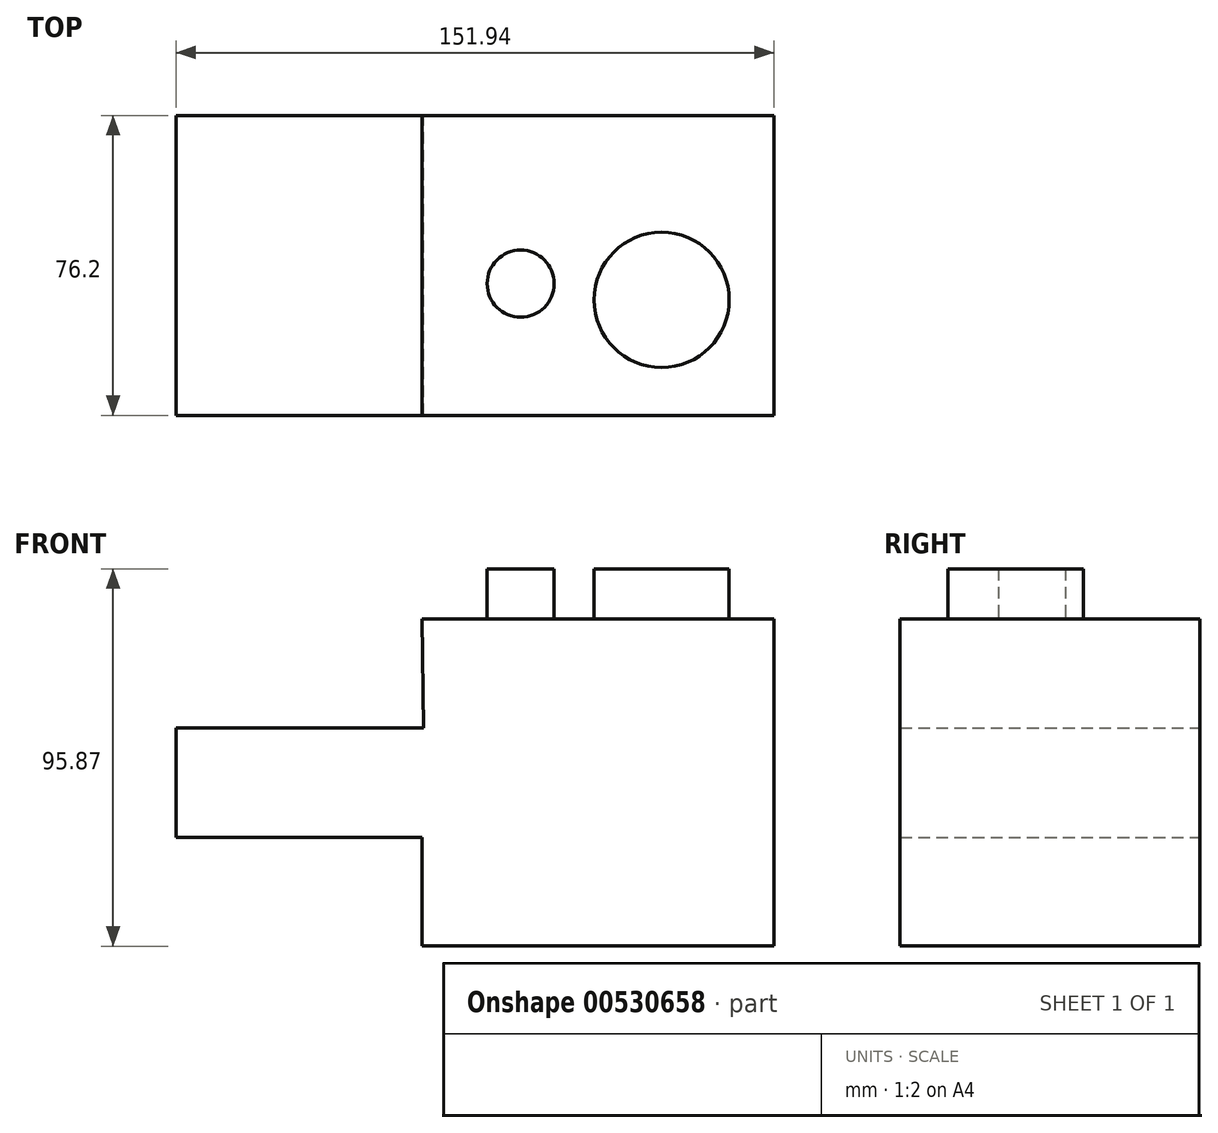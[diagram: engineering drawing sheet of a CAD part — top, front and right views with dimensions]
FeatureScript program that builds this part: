
annotation { "Feature Type Name" : "Feature", "Feature Type Description" : "" }
export const myFeature = defineFeature(function(context is Context, id is Id, definition is map)
    precondition{}
    {
        {
            var Q0;
            Q0=qCreatedBy(makeId("Front.planeOp"),FACE);
            var sketch = newSketch(context, id + "F0", { "sketchPlane" : qUnion([Q0])});
            skLineSegment(sketch, "E0.bottom", {"start": v(-81.39, 11.43) * mm, "end": v(-18.52, 11.43) * mm});
            skLineSegment(sketch, "E0.top", {"start": v(-81.39, -16.36) * mm, "end": v(-18.52, -16.36) * mm});
            skLineSegment(sketch, "E0.left", {"start": v(-81.39, 11.43) * mm, "end": v(-81.39, -16.36) * mm});
            skLineSegment(sketch, "E1.bottom", {"start": v(-18.92, 39.22) * mm, "end": v(70.55, 39.22) * mm});
            skLineSegment(sketch, "E1.top", {"start": v(-18.92, -43.95) * mm, "end": v(70.55, -43.95) * mm});
            skLineSegment(sketch, "E1.right", {"start": v(70.55, 39.22) * mm, "end": v(70.55, -43.95) * mm});
            skLineSegment(sketch, "E2.trimOffspring", {"start": v(-18.92, -16.36) * mm, "end": v(-18.92, -43.95) * mm});
            skLineSegment(sketch, "E3", {"start": v(-18.52, 11.43) * mm, "end": v(-18.92, 39.22) * mm});
            skSolve(sketch);
        }
        {
            var Q0;
            Q0=makeQuery(id+"F0.imprint","IMPRINT",FACE,{"disambiguationData":[TD([[makeQuery(id+"F0.imprint","IMPRINT",EDGE,{"derivedFrom":sQuery(id+"F0.wireOp",EDGE,"E0.bottom")}),-1.0]])]});
            extrude(context, id + "F1", {"entities" : qUnion([Q0]), "depth" : 76.2 * mm, "offsetDistance" : 25.4 * mm});
        }
        {
            var Q0;
            Q0=makeQuery(id+"F1.opExtrude","SWEPT_FACE",FACE,{"disambiguationData":[OSD([sQuery(id+"F0.wireOp",EDGE,"E1.bottom")])]});
            var sketch = newSketch(context, id + "F2", { "sketchPlane" : qUnion([Q0])});
            skCircle(sketch, "E4", {"center": v(41.94, -46.87) * mm, "radius": 17.18 * mm});
            skCircle(sketch, "E5", {"center": v(6.13, -42.75) * mm, "radius": 8.51 * mm});
            skSolve(sketch);
        }
        {
            var Q0;
            Q0 = qSketchRegion(id + "F2", true);
            extrude(context, id + "F3", {"entities" : qUnion([Q0]), "operationType" : NewBodyOperationType.ADD, "depth" : 12.7 * mm, "offsetDistance" : 25.4 * mm});
        }
    });
